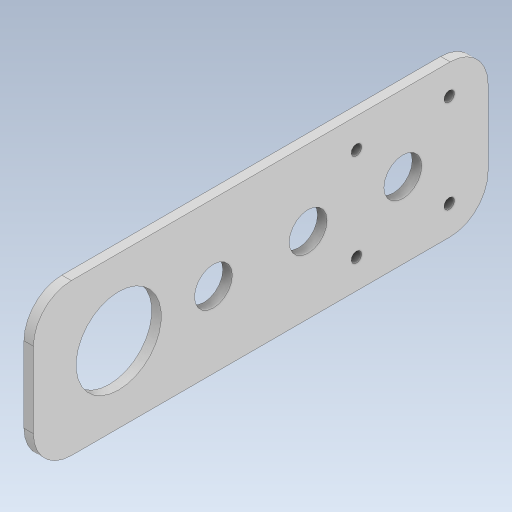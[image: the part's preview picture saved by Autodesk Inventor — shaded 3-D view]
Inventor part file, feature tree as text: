
AUTODESK INVENTOR PART (.ipt)
format: ipt  version: 2023 (Build 270158000, 158)  size: 135,680 bytes
history: native  units: in
note: dims shown in document units (in); Inventor stores cm internally (conversion verified against a paired STEP export)
features: extrude x1, sketch x1
ambient origin geometry x8: Origin, YZ Plane, XZ Plane, XY Plane, X Axis, Y Axis, Z Axis, Center Point
bodies: Solid1 (feature_tree)
feature tree (2):
  extrude  "Extrusion1"  Depth=6.0in
  sketch  "Sketch1"  dims[d0=2.0in d1=6.0in d2=0.5in d3=1.125in d4=0.5in d5=0.5in d6=0.5in d7=1.25in d8=1.25in d9=1.25in d10=1.7323in d11=0.1378in d12=1.5748in d14=360.0deg d16=0.125in d17=0.0in d18=0.5in d19=0.0344in d20=0.5in d21=0.0344in]
